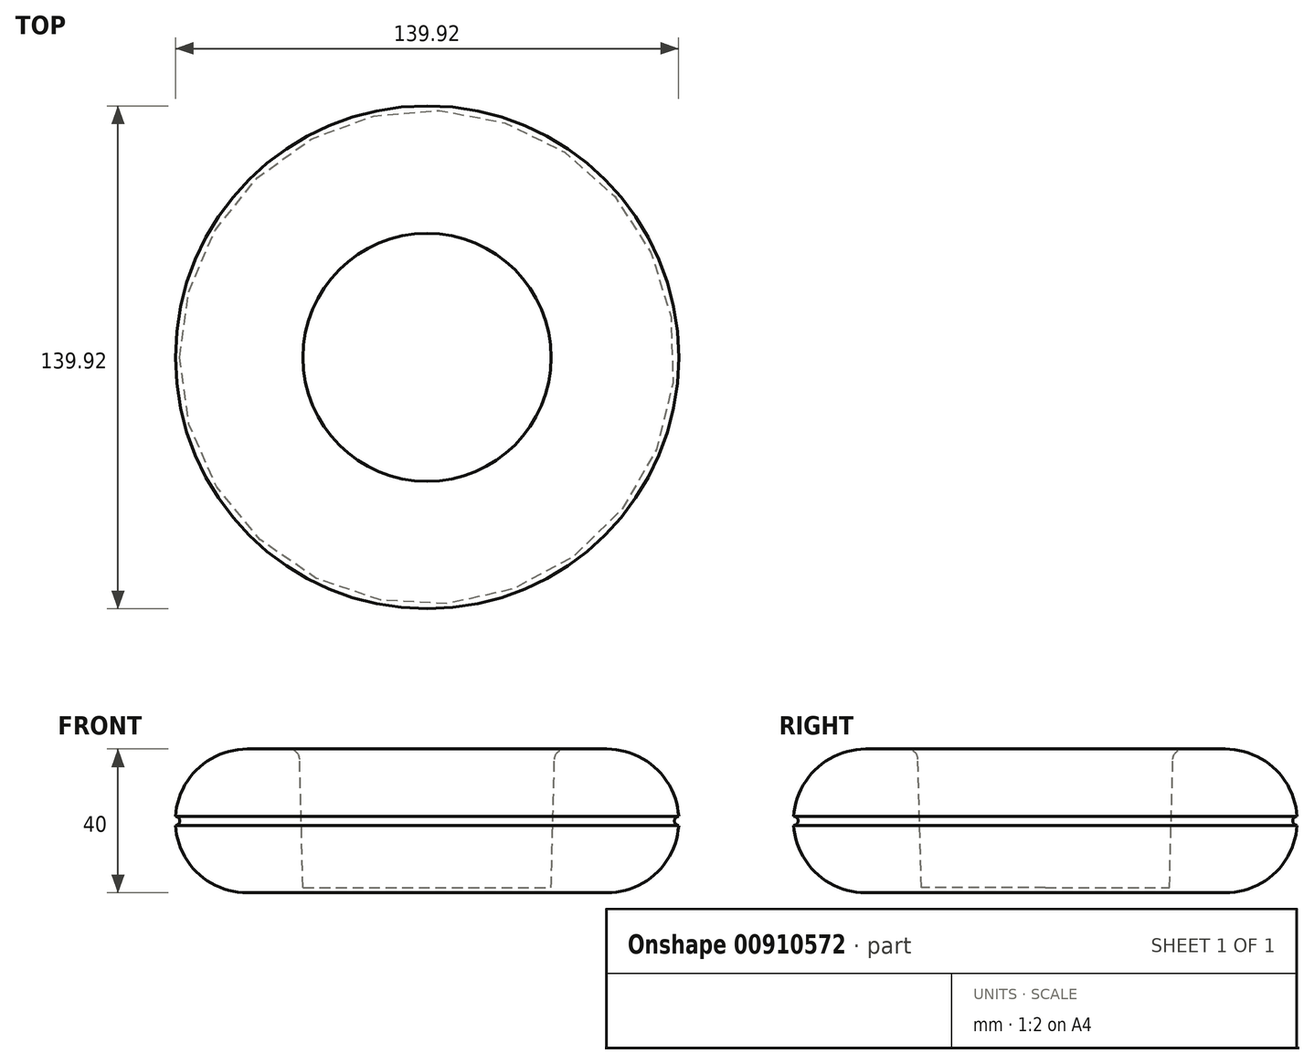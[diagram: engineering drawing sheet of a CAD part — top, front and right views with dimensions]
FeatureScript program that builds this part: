
annotation { "Feature Type Name" : "Feature", "Feature Type Description" : "" }
export const myFeature = defineFeature(function(context is Context, id is Id, definition is map)
    precondition{}
    {
        {
            var Q0;
            Q0=qCreatedBy(makeId("Front.planeOp"),FACE);
            var sketch = newSketch(context, id + "F0", { "sketchPlane" : qUnion([Q0])});
            skLineSegment(sketch, "E0.bottom", {"start": v(0, 0) * mm, "end": v(-50, 0) * mm});
            skLineSegment(sketch, "E0.top", {"start": v(-35.5, 40) * mm, "end": v(-50, 40) * mm});
            skLineSegment(sketch, "E0.left", {"start": v(0, 0) * mm, "end": v(0, 40) * mm});
            skArc(sketch, "E1", {"start": v(-50, 40) * mm, "mid": v(-63.7, 34.58) * mm, "end": v(-69.96, 21.25) * mm});
            skLineSegment(sketch, "E2", {"start": v(-50, 20) * mm, "end": v(-70, 20) * mm, "construction": true});
            skArc(sketch, "E3", {"start": v(-69.96, 18.75) * mm, "mid": v(-68.75, 20) * mm, "end": v(-69.96, 21.25) * mm});
            skArc(sketch, "E4.trimOffspring", {"start": v(-69.96, 18.75) * mm, "mid": v(-63.7, 5.42) * mm, "end": v(-50, 0) * mm});
            skLineSegment(sketch, "E5.trimOffspring", {"start": v(-71.25, 20) * mm, "end": v(-73.97, 20) * mm, "construction": true});
            skLineSegment(sketch, "E6.top", {"start": v(0, 1.5) * mm, "end": v(-34.5, 1.5) * mm});
            skLineSegment(sketch, "E6.left", {"start": v(0, 40) * mm, "end": v(0, 1.5) * mm});
            skLineSegment(sketch, "E7", {"start": v(-35.5, 40) * mm, "end": v(-34.5, 1.5) * mm});
            skPoint(sketch, "E8.orphan", {"position": v(-35.5, 1.5) * mm});
            skSolve(sketch);
        }
        {
            var Q0;
            Q0=makeQuery(id+"F0.imprint","IMPRINT",FACE,{"disambiguationData":[TD([[makeQuery(id+"F0.imprint","IMPRINT",EDGE,{"derivedFrom":sQuery(id+"F0.wireOp",EDGE,"E0.bottom")}),-1.0]])]});
            var Q1;
            Q1=sQuery(id+"F0.wireOp",EDGE,"E0.left");
            revolve(context, id + "F1", {"surfaceOperationType" : NewSurfaceOperationType.NEW, "entities" : qUnion([Q0]), "axis" : qUnion([Q1]), "revolveType" : RevolveType.FULL});
        }
        {
            var Q0;
            Q0=makeQuery(id+"F1.opRevolve","SWEPT_EDGE",EDGE,{"disambiguationData":[OSD([sQuery(id+"F0.wireOp",EDGE,"E0.top"),sQuery(id+"F0.wireOp",EDGE,"E7")])]});
            fillet(context, id + "F2", {"entities" : qUnion([Q0]), "radius" : 3 * mm, "tangentPropagation" : true, "allowEdgeOverflow" : false});
        }
    });
